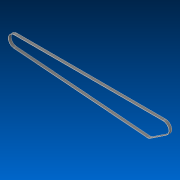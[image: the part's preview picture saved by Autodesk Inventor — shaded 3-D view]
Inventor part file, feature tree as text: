
AUTODESK INVENTOR PART (.ipt)
format: ipt  version: 2022 (Build 260153000, 153)  size: 107,520 bytes
history: native  units: in
note: dims shown in document units (in); Inventor stores cm internally (conversion verified against a paired STEP export)
features: extrude x1, sketch x1
ambient origin geometry x8: Origin, YZ Plane, XZ Plane, XY Plane, X Axis, Y Axis, Z Axis, Center Point
bodies: Solid1 (feature_tree)
feature tree (2):
  extrude  "Extrusion1"  Depth=0.3543in
  sketch  "Sketch1"  dims[d0=19.5in d1=1.504in d2=0.0394in d3=0.3543in d4=0.0in d5=0.875in d6=2.0in d7=1.715in]
